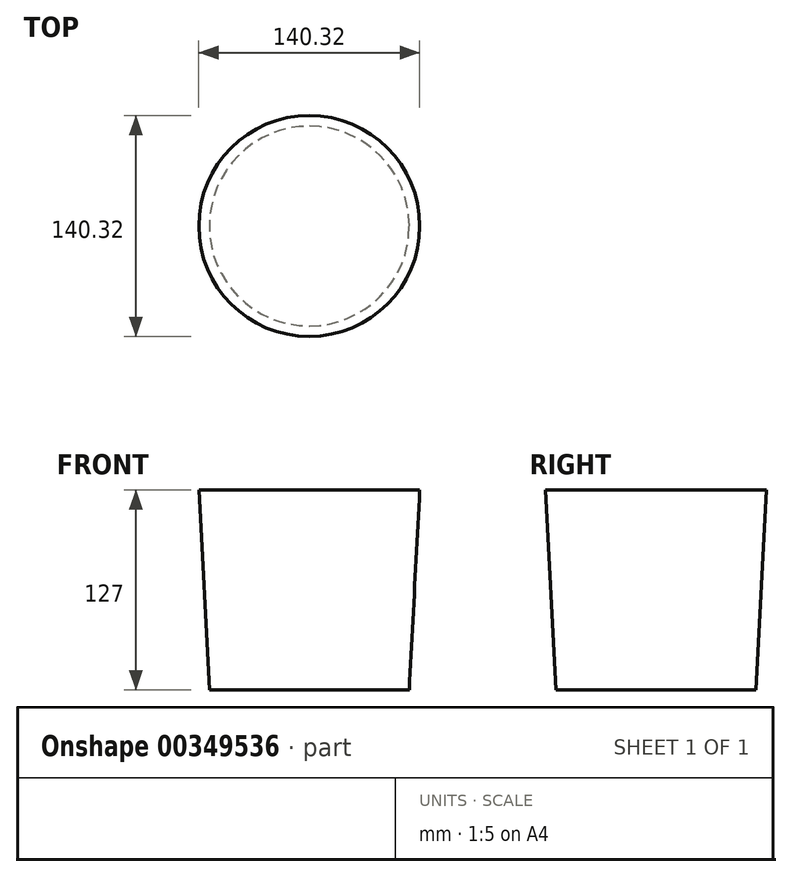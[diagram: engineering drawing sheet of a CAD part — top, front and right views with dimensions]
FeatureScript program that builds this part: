
annotation { "Feature Type Name" : "Feature", "Feature Type Description" : "" }
export const myFeature = defineFeature(function(context is Context, id is Id, definition is map)
    precondition{}
    {
        {
            var Q0;
            Q0=qCreatedBy(makeId("Top.planeOp"),FACE);
            var sketch = newSketch(context, id + "F0", { "sketchPlane" : qUnion([Q0])});
            skCircle(sketch, "E0", {"center": v(0, 0) * mm, "radius": 63.5 * mm});
            skSolve(sketch);
        }
        {
            var Q0;
            Q0 = qSketchRegion(id + "F0", true);
            extrude(context, id + "F1", {"entities" : qUnion([Q0]), "depth" : 127 * mm, "hasDraft" : true, "draftAngle" : 3 * degree});
        }
    });
